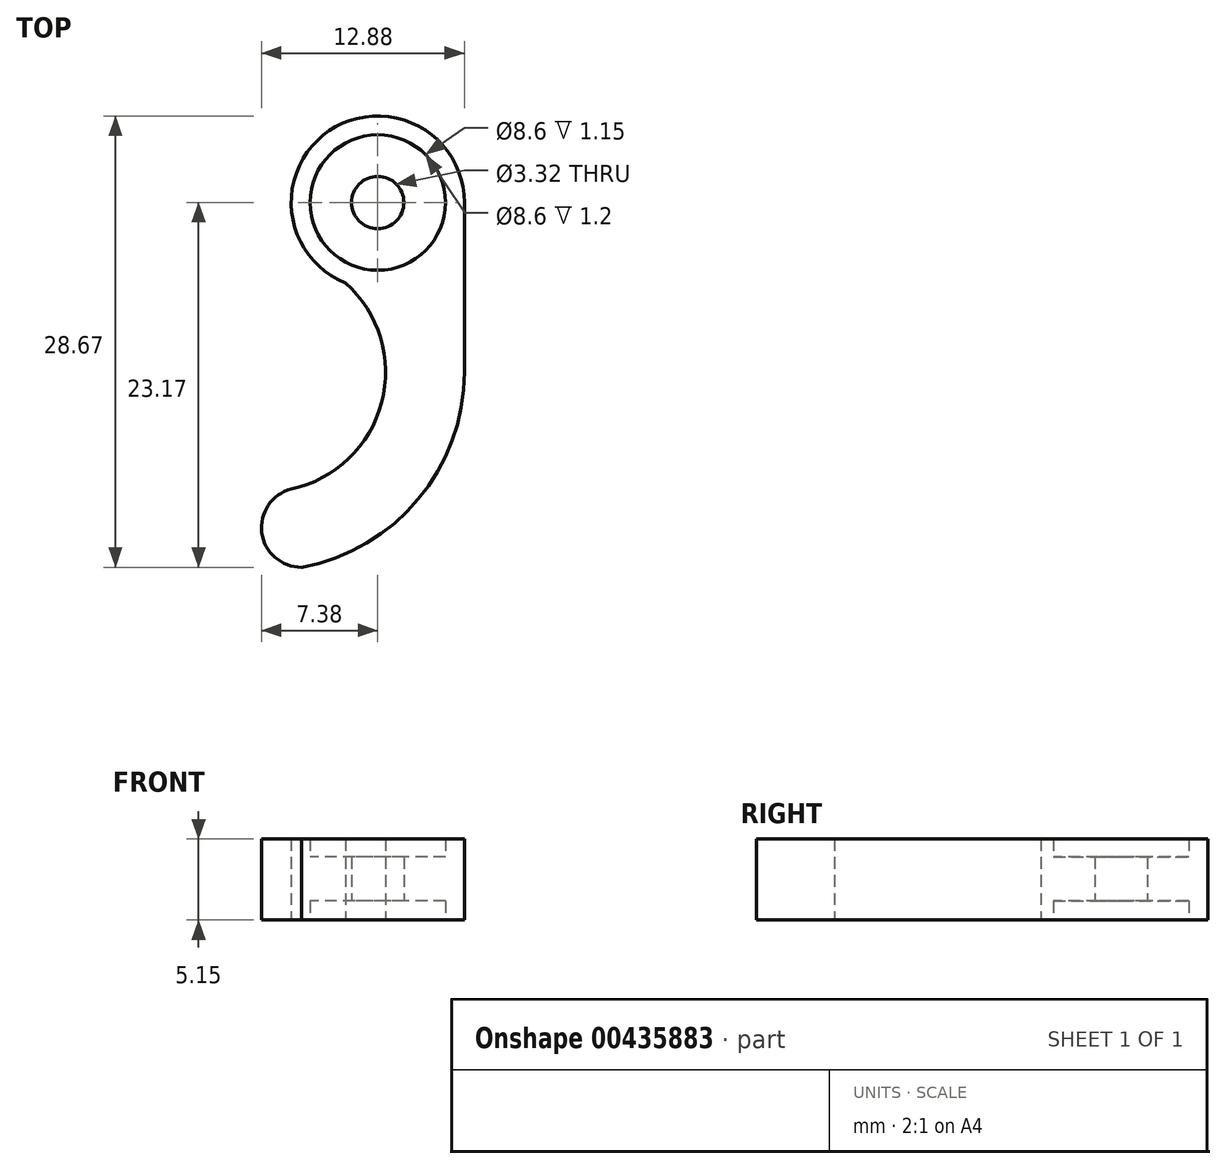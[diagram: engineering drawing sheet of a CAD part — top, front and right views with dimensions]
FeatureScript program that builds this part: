
annotation { "Feature Type Name" : "Feature", "Feature Type Description" : "" }
export const myFeature = defineFeature(function(context is Context, id is Id, definition is map)
    precondition{}
    {
        {
            var Q0;
            Q0=qCreatedBy(makeId("Top.planeOp"),FACE);
            var sketch = newSketch(context, id + "F0", { "sketchPlane" : qUnion([Q0])});
            skCircle(sketch, "E0", {"center": v(0, 0) * mm, "radius": 5.5 * mm});
            skCircle(sketch, "E1.0", {"center": v(0, 0) * mm, "radius": 4.3 * mm});
            skCircle(sketch, "E2", {"center": v(0, 0) * mm, "radius": 1.66 * mm});
            skLineSegment(sketch, "E3", {"start": v(5.5, 0) * mm, "end": v(5.5, -10.78) * mm});
            skLineSegment(sketch, "E4", {"start": v(-5.5, 0) * mm, "end": v(-5.5, -18.2) * mm, "construction": true});
            skArc(sketch, "E5", {"start": v(-5.5, -18.2) * mm, "mid": v(0.25, -12.71) * mm, "end": v(-2.05, -5.1) * mm});
            skArc(sketch, "E6.0", {"start": v(-4.84, -23.17) * mm, "mid": v(2.58, -18.85) * mm, "end": v(5.5, -10.78) * mm});
            skArc(sketch, "E7", {"start": v(-5.5, -18.2) * mm, "mid": v(-7.23, -21.5) * mm, "end": v(-3.8, -22.93) * mm});
            skSolve(sketch);
        }
        {
            var Q0;
            {var subQ1=sQuery(id+"F0.wireOp",EDGE,"E3");Q0=makeQuery(id+"F0.imprint","IMPRINT",FACE,{"disambiguationData":[TD([[makeQuery(id+"F0.imprint","IMPRINT",EDGE,{"derivedFrom":subQ1}),-1.0]])]});}
            var Q1;
            Q1=makeQuery(id+"F0.imprint","IMPRINT",FACE,{"disambiguationData":[TD([[makeQuery(id+"F0.imprint","IMPRINT",EDGE,{"derivedFrom":sQuery(id+"F0.wireOp",EDGE,"E1.0")}),-1.0]])]});
            extrude(context, id + "F1", {"entities" : qUnion([Q0, Q1]), "depth" : 5.15 * mm});
        }
        {
            var Q0;
            Q0=makeQuery(id+"F0.imprint","IMPRINT",FACE,{"disambiguationData":[TD([[makeQuery(id+"F0.imprint","IMPRINT",EDGE,{"derivedFrom":sQuery(id+"F0.wireOp",EDGE,"E1.0")}),1.0]])]});
            extrude(context, id + "F2", {"entities" : qUnion([Q0]), "operationType" : NewBodyOperationType.ADD, "depth" : 4 * mm});
        }
        {
            var Q0;
            Q0=makeQuery(id+"F0.imprint","IMPRINT",FACE,{"disambiguationData":[TD([[makeQuery(id+"F0.imprint","IMPRINT",EDGE,{"derivedFrom":sQuery(id+"F0.wireOp",EDGE,"E1.0")}),1.0]])]});
            extrude(context, id + "F3", {"entities" : qUnion([Q0]), "operationType" : NewBodyOperationType.REMOVE, "depth" : 1.2 * mm});
        }
    });
